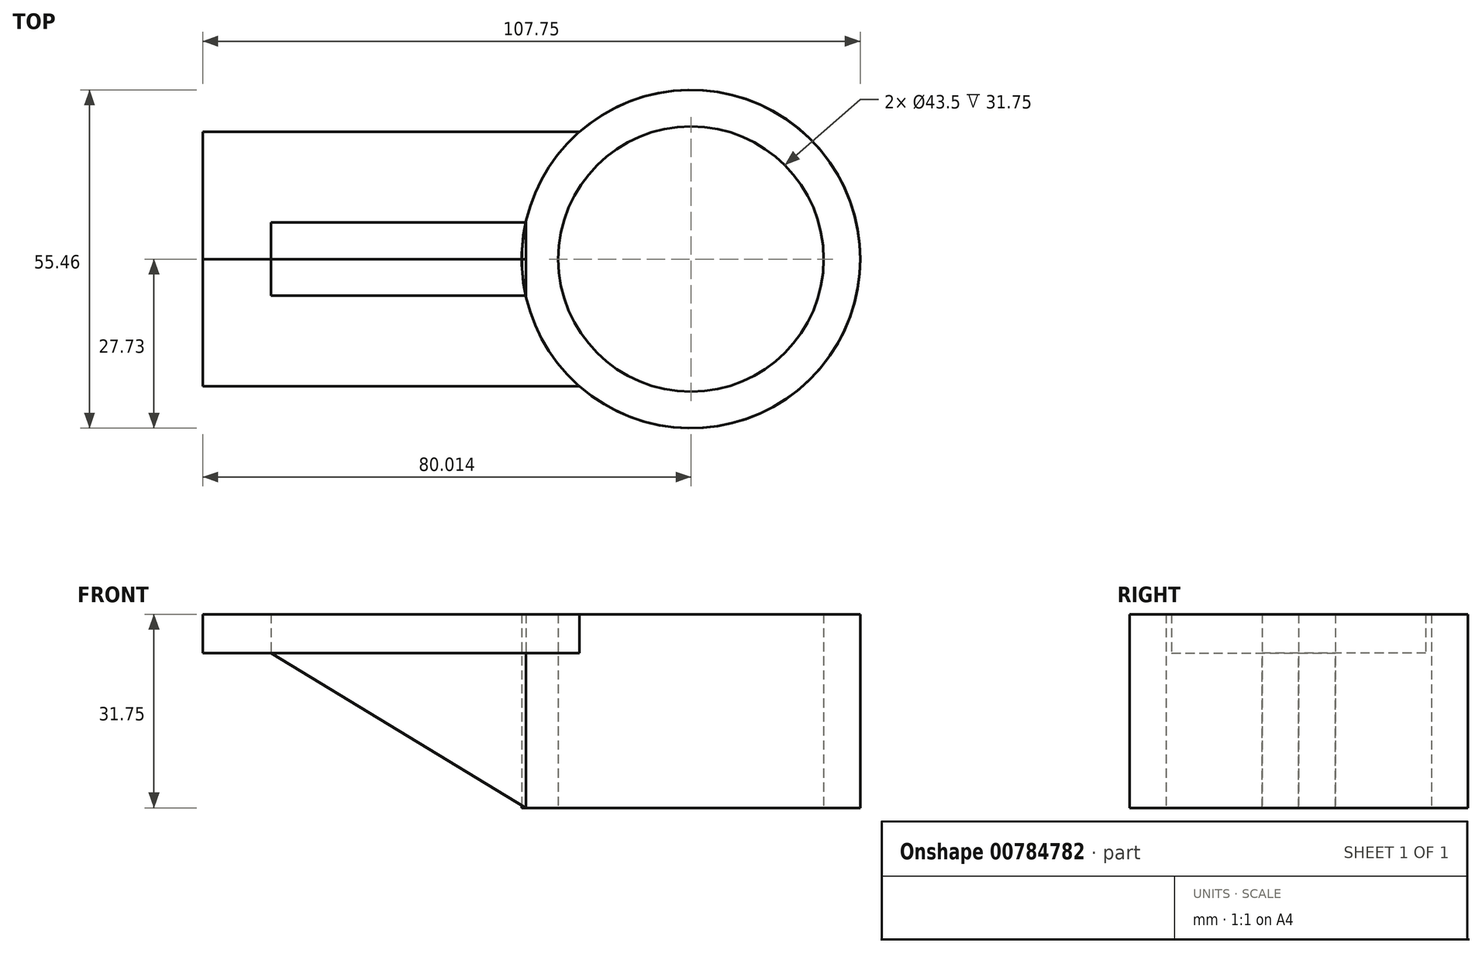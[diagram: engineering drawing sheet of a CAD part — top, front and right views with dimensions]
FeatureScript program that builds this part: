
annotation { "Feature Type Name" : "Feature", "Feature Type Description" : "" }
export const myFeature = defineFeature(function(context is Context, id is Id, definition is map)
    precondition{}
    {
        {
            var Q0;
            Q0=qCreatedBy(makeId("Top.planeOp"),FACE);
            var sketch = newSketch(context, id + "F0", { "sketchPlane" : qUnion([Q0])});
            skCircle(sketch, "E0", {"center": v(39.3, 0) * mm, "radius": 27.73 * mm});
            skLineSegment(sketch, "E1", {"start": v(21, 20.84) * mm, "end": v(-40.72, 20.84) * mm});
            skLineSegment(sketch, "E2", {"start": v(-40.72, 20.84) * mm, "end": v(-40.72, 0) * mm});
            skLineSegment(sketch, "E3", {"start": v(-40.72, 0) * mm, "end": v(11.56, 0) * mm});
            skCircle(sketch, "E4", {"center": v(39.3, 0) * mm, "radius": 21.75 * mm});
            skLineSegment(sketch, "E5", {"start": v(-29.55, 0) * mm, "end": v(-29.55, 6) * mm});
            skLineSegment(sketch, "E6", {"start": v(-29.55, 6) * mm, "end": v(12.22, 6) * mm});
            skLineSegment(sketch, "E7", {"start": v(11.56, 0) * mm, "end": v(67.03, 0) * mm});
            skSolve(sketch);
        }
        {
            var Q0;
            {var subQ1=sQuery(id+"F0.wireOp",EDGE,"E1");Q0=makeQuery(id+"F0.imprint","IMPRINT",FACE,{"disambiguationData":[TD([[makeQuery(id+"F0.imprint","IMPRINT",EDGE,{"derivedFrom":subQ1}),1.0]])]});}
            extrude(context, id + "F1", {"entities" : qUnion([Q0]), "depth" : 6.35 * mm, "offsetDistance" : 25.4 * mm});
        }
        {
            var Q0;
            {var subQ4=sQuery(id+"F0.wireOp",EDGE,"E0");var subQ7=makeQuery(id+"F0.imprint","INTERSECT",VERTEX,{"derivedFrom":[subQ4,sQuery(id+"F0.wireOp",EDGE,"E1")]});Q0=makeQuery(id+"F0.imprint","IMPRINT",FACE,{"disambiguationData":[TD([[makeQuery(id+"F0.imprint","IMPRINT",EDGE,{"disambiguationData":[TD([[subQ7,1.0]])],"derivedFrom":subQ4}),1.0]])]});}
            var Q1;
            {var subQ0=sQuery(id+"F0.wireOp",EDGE,"E7");var subQ4=sQuery(id+"F0.wireOp",EDGE,"E4");var subQ5=makeQuery(id+"F0.imprint","INTERSECT",VERTEX,{"disambiguationData":[OD(0.0)],"derivedFrom":[subQ4,subQ0]});Q1=makeQuery(id+"F0.imprint","IMPRINT",FACE,{"disambiguationData":[TD([[makeQuery(id+"F0.imprint","IMPRINT",EDGE,{"disambiguationData":[TD([[subQ5,-1.0]])],"derivedFrom":subQ4}),-1.0]])]});}
            extrude(context, id + "F2", {"entities" : qUnion([Q0, Q1]), "operationType" : NewBodyOperationType.ADD, "depth" : 6.35 * mm, "offsetDistance" : 25.4 * mm});
        }
        {
            var Q0;
            {var subQ4=sQuery(id+"F0.wireOp",EDGE,"E0");var subQ7=makeQuery(id+"F0.imprint","INTERSECT",VERTEX,{"derivedFrom":[subQ4,sQuery(id+"F0.wireOp",EDGE,"E1")]});Q0=makeQuery(id+"F0.imprint","IMPRINT",FACE,{"disambiguationData":[TD([[makeQuery(id+"F0.imprint","IMPRINT",EDGE,{"disambiguationData":[TD([[subQ7,1.0]])],"derivedFrom":subQ4}),1.0]])]});}
            var Q1;
            {var subQ0=sQuery(id+"F0.wireOp",EDGE,"E7");var subQ4=sQuery(id+"F0.wireOp",EDGE,"E4");var subQ5=makeQuery(id+"F0.imprint","INTERSECT",VERTEX,{"disambiguationData":[OD(0.0)],"derivedFrom":[subQ4,subQ0]});Q1=makeQuery(id+"F0.imprint","IMPRINT",FACE,{"disambiguationData":[TD([[makeQuery(id+"F0.imprint","IMPRINT",EDGE,{"disambiguationData":[TD([[subQ5,-1.0]])],"derivedFrom":subQ4}),-1.0]])]});}
            extrude(context, id + "F3", {"entities" : qUnion([Q0, Q1]), "operationType" : NewBodyOperationType.ADD, "oppositeDirection" : true, "depth" : 25.4 * mm, "offsetDistance" : 25.4 * mm});
        }
        {
            var Q0;
            Q0=makeQuery(id+"F1.opExtrude","SWEPT_FACE",FACE,{"disambiguationData":[OSD([sQuery(id+"F0.wireOp",EDGE,"E6")])]});
            var sketch = newSketch(context, id + "F4", { "sketchPlane" : qUnion([Q0])});
            skLineSegment(sketch, "E8", {"start": v(12.22, 0) * mm, "end": v(12.22, -25.4) * mm});
            skLineSegment(sketch, "E9", {"start": v(12.22, -25.4) * mm, "end": v(-29.55, 0) * mm});
            skLineSegment(sketch, "E10", {"start": v(12.22, 0) * mm, "end": v(-29.55, 0) * mm});
            skLineSegment(sketch, "E11", {"start": v(12.22, 0) * mm, "end": v(12.22, 6.35) * mm});
            skLineSegment(sketch, "E12", {"start": v(-29.55, 6.35) * mm, "end": v(12.22, 6.35) * mm});
            skLineSegment(sketch, "E13", {"start": v(-29.55, 6.35) * mm, "end": v(-29.55, 0) * mm});
            skSolve(sketch);
        }
        {
            var Q0;
            Q0 = qSketchRegion(id + "F4", true);
            extrude(context, id + "F5", {"entities" : qUnion([Q0]), "depth" : 6 * mm, "offsetDistance" : 25.4 * mm});
        }
        {
            var Q0;
            Q0=makeQuery(id+"F1.opExtrude","SWEPT_BODY",BODY,{"disambiguationData":[OSD([sQuery(id+"F0.wireOp",EDGE,"E0"),sQuery(id+"F0.wireOp",EDGE,"E1"),sQuery(id+"F0.wireOp",EDGE,"E2"),sQuery(id+"F0.wireOp",EDGE,"E3"),sQuery(id+"F0.wireOp",EDGE,"E5"),sQuery(id+"F0.wireOp",EDGE,"E6")])]});
            var Q1;
            Q1=makeQuery(id+"F5.opExtrude","SWEPT_BODY",BODY,{"disambiguationData":[OSD([sQuery(id+"F4.wireOp",EDGE,"E8"),sQuery(id+"F4.wireOp",EDGE,"E9"),sQuery(id+"F4.wireOp",EDGE,"E11"),sQuery(id+"F4.wireOp",EDGE,"E12"),sQuery(id+"F4.wireOp",EDGE,"E13")])]});
            var Q2;
            Q2=qCreatedBy(makeId("Front.planeOp"),FACE);
            mirror(context, id + "F6", {"entities" : qUnion([Q0, Q1]), "mirrorPlane" : qUnion([Q2])});
        }
    });
